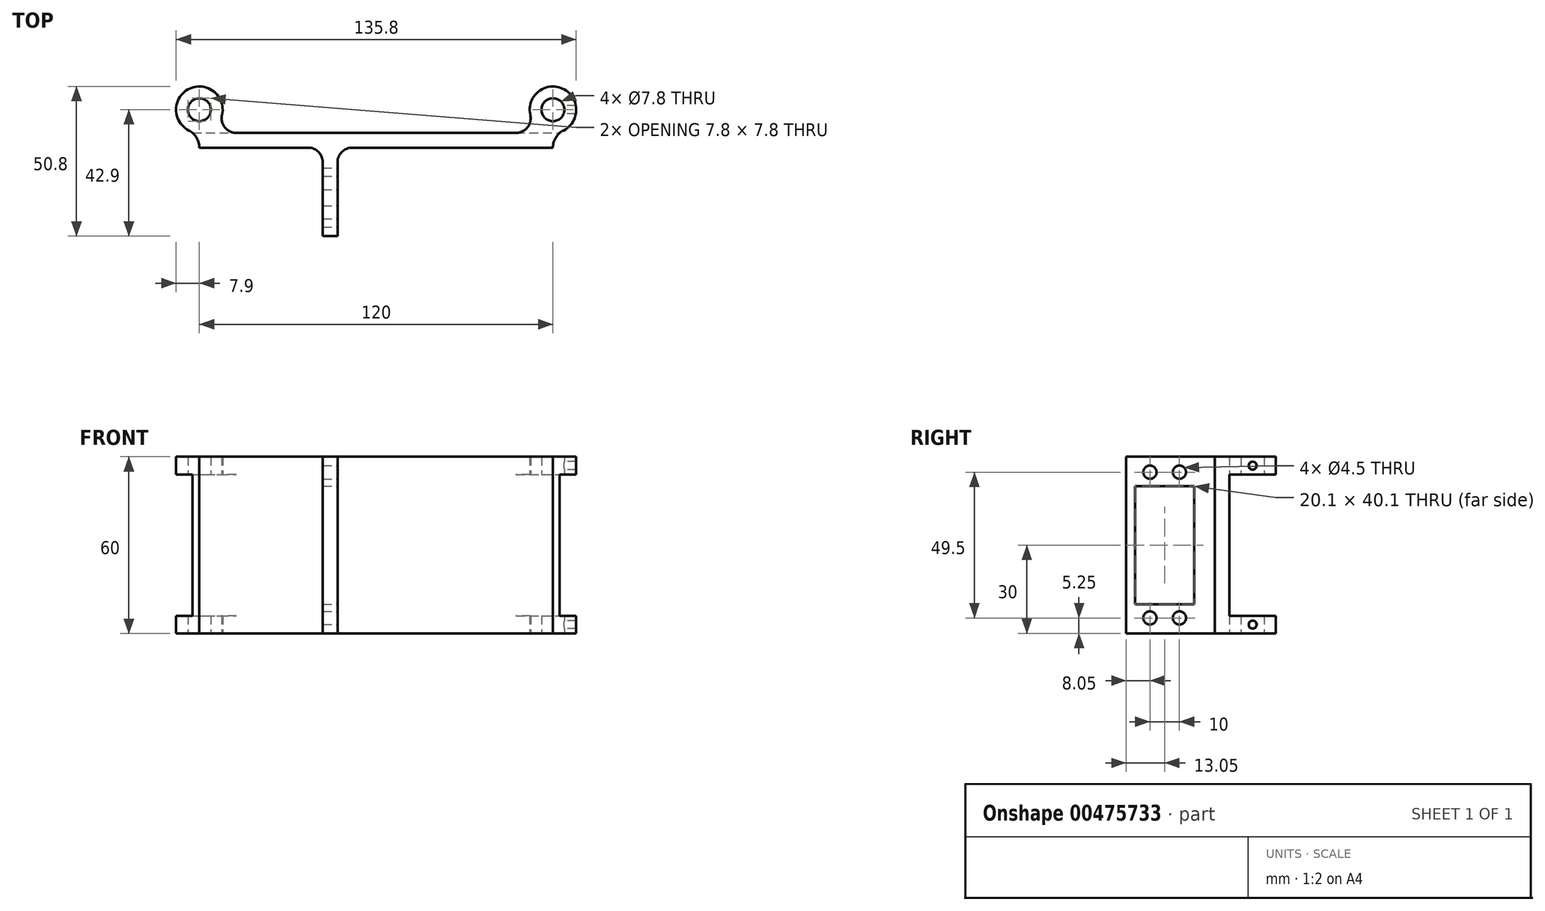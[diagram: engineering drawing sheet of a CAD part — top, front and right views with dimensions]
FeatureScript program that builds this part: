
annotation { "Feature Type Name" : "Feature", "Feature Type Description" : "" }
export const myFeature = defineFeature(function(context is Context, id is Id, definition is map)
    precondition{}
    {
        {
            var Q0;
            Q0=qCreatedBy(makeId("Top.planeOp"),FACE);
            var sketch = newSketch(context, id + "F0", { "sketchPlane" : qUnion([Q0])});
            skLineSegment(sketch, "E0.bottom", {"start": v(-60, 0) * mm, "end": v(60, 0) * mm});
            skLineSegment(sketch, "E0.top", {"start": v(-60, -5) * mm, "end": v(60, -5) * mm});
            skLineSegment(sketch, "E0.left", {"start": v(-60, 0) * mm, "end": v(-60, -5) * mm});
            skLineSegment(sketch, "E0.right", {"start": v(60, 0) * mm, "end": v(60, -5) * mm});
            skCircle(sketch, "E1", {"center": v(60, 7.9) * mm, "radius": 7.9 * mm});
            skCircle(sketch, "E2", {"center": v(-60, 7.9) * mm, "radius": 7.9 * mm});
            skCircle(sketch, "E3", {"center": v(-60, 7.9) * mm, "radius": 3.9 * mm});
            skCircle(sketch, "E4", {"center": v(60, 7.9) * mm, "radius": 3.9 * mm});
            skArc(sketch, "E5", {"start": v(-52.3, 6.12) * mm, "mid": v(-51.34, 1.89) * mm, "end": v(-47.43, 0) * mm});
            skArc(sketch, "E6", {"start": v(-60, -5) * mm, "mid": v(-60.97, -1.56) * mm, "end": v(-63.6, 0.86) * mm});
            skArc(sketch, "E7", {"start": v(47.43, 0) * mm, "mid": v(51.34, 1.89) * mm, "end": v(52.3, 6.12) * mm});
            skArc(sketch, "E8", {"start": v(63.6, 0.86) * mm, "mid": v(60.97, -1.56) * mm, "end": v(60, -5) * mm});
            skLineSegment(sketch, "E9.bottom", {"start": v(-18.1, -5) * mm, "end": v(-13.1, -5) * mm});
            skLineSegment(sketch, "E9.top", {"start": v(-18.1, -35) * mm, "end": v(-13.1, -35) * mm});
            skLineSegment(sketch, "E9.left", {"start": v(-18.1, -5) * mm, "end": v(-18.1, -35) * mm});
            skLineSegment(sketch, "E9.right", {"start": v(-13.1, -5) * mm, "end": v(-13.1, -35) * mm});
            skSolve(sketch);
        }
        {
            var Q0;
            Q0=qSketchRegion(id+"F0",true);
            extrude(context, id + "F1", {"entities" : qUnion([Q0]), "depth" : 60 * mm});
        }
        {
            var Q0;
            Q0=makeQuery(id+"F1.opExtrude","SWEPT_FACE",FACE,{"disambiguationData":[OSD([sQuery(id+"F0.wireOp",EDGE,"E9.right")])]});
            var sketch = newSketch(context, id + "F2", { "sketchPlane" : qUnion([Q0])});
            skLineSegment(sketch, "E10.bottom", {"start": v(-32, 50.05) * mm, "end": v(-11.9, 50.05) * mm});
            skLineSegment(sketch, "E10.top", {"start": v(-32, 9.95) * mm, "end": v(-11.9, 9.95) * mm});
            skLineSegment(sketch, "E10.left", {"start": v(-32, 50.05) * mm, "end": v(-32, 9.95) * mm});
            skLineSegment(sketch, "E10.right", {"start": v(-11.9, 50.05) * mm, "end": v(-11.9, 9.95) * mm});
            skLineSegment(sketch, "E11", {"start": v(-32, 30) * mm, "end": v(-11.9, 30) * mm, "construction": true});
            skLineSegment(sketch, "E12", {"start": v(-21.95, 50.05) * mm, "end": v(-21.95, 9.95) * mm, "construction": true});
            skCircle(sketch, "E13", {"center": v(-26.95, 54.75) * mm, "radius": 2.25 * mm});
            skCircle(sketch, "E14.MirrorC", {"center": v(-16.95, 54.75) * mm, "radius": 2.25 * mm});
            skCircle(sketch, "E15.MirrorC", {"center": v(-16.95, 5.25) * mm, "radius": 2.25 * mm});
            skCircle(sketch, "E16.MirrorC", {"center": v(-26.95, 5.25) * mm, "radius": 2.25 * mm});
            skSolve(sketch);
        }
        {
            var Q0;
            Q0=qSketchRegion(id+"F2",true);
            extrude(context, id + "F3", {"entities" : qUnion([Q0]), "operationType" : NewBodyOperationType.REMOVE, "endBound" : BoundingType.THROUGH_ALL, "oppositeDirection" : true, "depth" : 25 * mm});
        }
        {
            var Q0;
            Q0=makeQuery(id+"F1.opExtrude","CAP_FACE",FACE,{"disambiguationData":[OSD([sQuery(id+"F0.wireOp",EDGE,"E0.bottom"),sQuery(id+"F0.wireOp",EDGE,"E0.top"),sQuery(id+"F0.wireOp",EDGE,"E1"),sQuery(id+"F0.wireOp",EDGE,"E2"),sQuery(id+"F0.wireOp",EDGE,"E3"),sQuery(id+"F0.wireOp",EDGE,"E4"),sQuery(id+"F0.wireOp",EDGE,"E5"),sQuery(id+"F0.wireOp",EDGE,"E6"),sQuery(id+"F0.wireOp",EDGE,"E7"),sQuery(id+"F0.wireOp",EDGE,"E8"),sQuery(id+"F0.wireOp",EDGE,"E9.top"),sQuery(id+"F0.wireOp",EDGE,"E9.left"),sQuery(id+"F0.wireOp",EDGE,"E9.right")])],"isStart":false});
            var sketch = newSketch(context, id + "F4", { "sketchPlane" : qUnion([Q0])});
            skLineSegment(sketch, "E17.bottom", {"start": v(-79.7, -5) * mm, "end": v(82.75, -5) * mm});
            skLineSegment(sketch, "E17.top", {"start": v(-79.7, 30.92) * mm, "end": v(82.75, 30.92) * mm});
            skLineSegment(sketch, "E17.left", {"start": v(-79.7, -5) * mm, "end": v(-79.7, 30.92) * mm});
            skLineSegment(sketch, "E17.right", {"start": v(82.75, -5) * mm, "end": v(82.75, 30.92) * mm});
            skSolve(sketch);
        }
        {
            var Q0;
            Q0=qCreatedBy(makeId("Right.planeOp"),FACE);
            var sketch = newSketch(context, id + "F5", { "sketchPlane" : qUnion([Q0])});
            skLineSegment(sketch, "E18.0.1", {"start": v(0, 0) * mm, "end": v(0, 60) * mm});
            skLineSegment(sketch, "E18.0.3", {"start": v(0, 60) * mm, "end": v(0, 0) * mm});
            skLineSegment(sketch, "E19.bottom", {"start": v(0, 54) * mm, "end": v(34.22, 54) * mm});
            skLineSegment(sketch, "E19.top", {"start": v(0, 6) * mm, "end": v(34.22, 6) * mm});
            skLineSegment(sketch, "E19.left", {"start": v(0, 54) * mm, "end": v(0, 6) * mm});
            skLineSegment(sketch, "E19.right", {"start": v(34.22, 54) * mm, "end": v(34.22, 6) * mm});
            skLineSegment(sketch, "E20", {"start": v(0, 60) * mm, "end": v(0, 54) * mm, "construction": true});
            skLineSegment(sketch, "E21", {"start": v(0, 6) * mm, "end": v(0, 0) * mm, "construction": true});
            skSolve(sketch);
        }
        {
            var Q0;
            Q0=qSketchRegion(id+"F5",true);
            extrude(context, id + "F6", {"entities" : qUnion([Q0]), "operationType" : NewBodyOperationType.REMOVE, "endBound" : BoundingType.THROUGH_ALL, "oppositeDirection" : true, "depth" : 25 * mm, "hasSecondDirection" : true, "secondDirectionBound" : SecondDirectionBoundingType.THROUGH_ALL, "secondDirectionOppositeDirection" : false, "secondDirectionDepth" : 25 * mm});
        }
        {
            var Q0;
            Q0=makeQuery(id+"F1.opExtrude","SWEPT_EDGE",EDGE,{"disambiguationData":[OSD([sQuery(id+"F0.wireOp",EDGE,"E0.top"),sQuery(id+"F0.wireOp",EDGE,"E9.bottom"),sQuery(id+"F0.wireOp",EDGE,"E9.right")])]});
            var Q1;
            Q1=makeQuery(id+"F1.opExtrude","SWEPT_EDGE",EDGE,{"disambiguationData":[OSD([sQuery(id+"F0.wireOp",EDGE,"E0.top"),sQuery(id+"F0.wireOp",EDGE,"E9.bottom"),sQuery(id+"F0.wireOp",EDGE,"E9.left")])]});
            fillet(context, id + "F7", {"entities" : qUnion([Q0, Q1]), "radius" : 5 * mm, "tangentPropagation" : true, "allowEdgeOverflow" : false});
        }
        {
            var Q0;
            Q0=qCreatedBy(makeId("Right.planeOp"),FACE);
            cPlane(context, id + "F8", {"entities" : qUnion([Q0]), "cplaneType" : CPlaneType.OFFSET, "offset" : 60 * mm, "width" : 150 * mm, "height" : 150 * mm});
        }
        {
            var Q0;
            Q0=qCreatedBy(id+"F8.planeOp",FACE);
            var sketch = newSketch(context, id + "F9", { "sketchPlane" : qUnion([Q0])});
            skLineSegment(sketch, "E22", {"start": v(4, 54) * mm, "end": v(4, 60) * mm});
            skLineSegment(sketch, "E23", {"start": v(11.8, 60) * mm, "end": v(11.8, 54) * mm});
            skLineSegment(sketch, "E24", {"start": v(4, 0) * mm, "end": v(4, 6) * mm});
            skLineSegment(sketch, "E25", {"start": v(11.8, 6) * mm, "end": v(11.8, 0) * mm});
            skLineSegment(sketch, "E26", {"start": v(11.8, 57) * mm, "end": v(4, 57) * mm, "construction": true});
            skLineSegment(sketch, "E27", {"start": v(4, 3) * mm, "end": v(11.8, 3) * mm, "construction": true});
            skCircle(sketch, "E28", {"center": v(7.9, 57) * mm, "radius": 1.35 * mm});
            skCircle(sketch, "E29", {"center": v(7.9, 3) * mm, "radius": 1.35 * mm});
            skSolve(sketch);
        }
        {
            var Q0;
            Q0=qSketchRegion(id+"F9",true);
            extrude(context, id + "F10", {"entities" : qUnion([Q0]), "operationType" : NewBodyOperationType.REMOVE, "endBound" : BoundingType.THROUGH_ALL, "depth" : 25 * mm});
        }
    });
